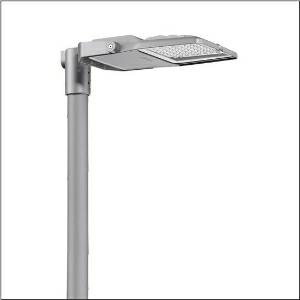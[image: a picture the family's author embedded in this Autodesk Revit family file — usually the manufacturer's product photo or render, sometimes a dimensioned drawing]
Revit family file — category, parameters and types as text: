
# Revit family: floodlight_fl_21_iq_mini___pl33t_5xa7772b4f3a_8cfb
name_source: partatom
category: Lighting Fixtures
units: mm (PartAtom-declared; Revit-internal decimal feet)

## family parameters
Cut with Voids When Loaded = No
Host = Face
Light Source = No
Part Type = Normal
Room Calculation Point = No
Round Connector Dimension = Use Diameter
Shared = No

## types (1)
- --- (1 x LED, 6420 lm, 45.5 W, 4000K)
    Apparent Load = 46 VA
    CIE Flux Codes = 26 75 99 100 100
    Color Rendering = 70
    Color Temperature = 4000K
    Default Elevation = 1800 mm
    Description = Floodlight FL 21 iQ mini, floodlight, primary light control with lens, of PMMA, primary optical cover: protective disc, of toughened safety glass, transparent, light distribution: PL33T, light emission: direct distribution, installation type: surface-mounted, LED, High Power LED, rated luminous flux: 6.420lm, luminous efficacy: 141lm/W, light colour: 740, colour temperature: 4000K, control gear: iQ Street-Remote/DALI, control: Auto-Match, Temp-Guard, Night-Set, Smart-Wire, Desk-Remote (wireless, voltage-free reading and setting of iQ features in the workshop via application-optimized NFC function/RFID function), optimised constant luminous flux control (CLO 2.0), Light-Fading, Lumen-Switch, with terminal, 6-pole, mains connection: 220..240V, AC, 50/60Hz, start of lifetime: 46W, end of service life: 48W, reduction: 22W, luminaire housing, of diecast aluminium, powder-coated, Siteco® metallic grey (DB 702S), corrosivity category C5 mid according to DIN EN ISO 12944, suitable for swimming pools, chlorine-resistant, sealing non-destructively replaceable, please order mast flange separately, mast bracket, of steel, galvanised, powder-coated, protection rating (complete): IP66, insulation class (complete): insulation class II (safety insulation), certification: CE, ENEC, VDE, protection symbol: D, impact resistance: IK08, permissible operating ambient temperature: -40..+40°C, permissible operating ambient temperature for outdoor applications: -40..+50°C, standard: DIN EN 12944, LABS conformity tested according to VDMA 24364:2018-05, packaging unit: 1 piece

Light Distribution: PL33T
    Height = 70 mm
    Lamp = 1 x LED
    Lamp Light Flux = 6420 lm
    Lamp Power = 45.5 W
    Lamp count = 1
    Length = 485 mm
    Luminous efficacy = 141 lm/W
    Manufacturer = Siteco
    ModVariant = No
    Model = 5XA7772B4F3A
    Number of Poles = 1
    OnlyDefault = Yes
    Power Factor = 1
    Product Name = Floodlight FL 21 iQ mini | PL33T
    Product group = floodlight | pylon annexe
    ProductGroupID = 6200
    Protection Class = Protection class II
    Protection Degree = IP 66
    RLX_Detail_Level = 1
    RLX_Emergency_Light_Flux = 0 lm
    RLX_Emergency_Type = 0
    RLX_Emergency_Type_DB = No
    RlxData = <blob elided: 101105 chars, md5=fb2c485a>
    Socket = socket
    Standby Power = 0 W
    System Light Flux = 6420 lm
    System Power = 46 W
    Type Comments = factory setting: luminous flux: 100 % | dim-lin: 254 | 463 mA
    Type Image = l_1007125.jpg
    URL = http://relux.com
    VarID = @adj_149888
    Voltage = 0 V
    Weight = 0.00 kg
    Width = 337 mm

## geometry (parser evidence)
native form markers: Blend x4, Sweep x12
no freeform markers — native parametric forms only
